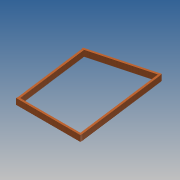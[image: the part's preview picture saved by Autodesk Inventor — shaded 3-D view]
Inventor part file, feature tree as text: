
AUTODESK INVENTOR PART (.ipt)
format: ipt  version: 2014 SP1 (Build 180222100, 222)  size: 108,544 bytes
history: native  units: in
note: dims shown in document units (in); Inventor stores cm internally (conversion verified against a paired STEP export)
features: extrude x3, sketch x3
ambient origin geometry x8: Origin, YZ Plane, XZ Plane, XY Plane, X Axis, Y Axis, Z Axis, Center Point
bodies: Solid1 (feature_tree)
feature tree (6):
  extrude  "Extrusion1"  Depth=1.4961in
  extrude  "Extrusion2"  Depth=0.0394in TaperAngle=0.0deg
  extrude  "Extrusion4"  [1 undecoded]
  sketch  "Sketch1"  dims[d7=1.4961in d8=1.4961in]
  sketch  "Sketch2"  dims[d9=4.4882in d10=0.0in d11=0.0394in d12=0.0in]
  sketch  "Sketch4"  dims[d15=0.0394in d16=0.0in]
note: 1 required parameter value undecoded (feature->parameter linkage not recoverable at this tier; creation-order binding heuristic only, values carry confidence <= 0.55)
